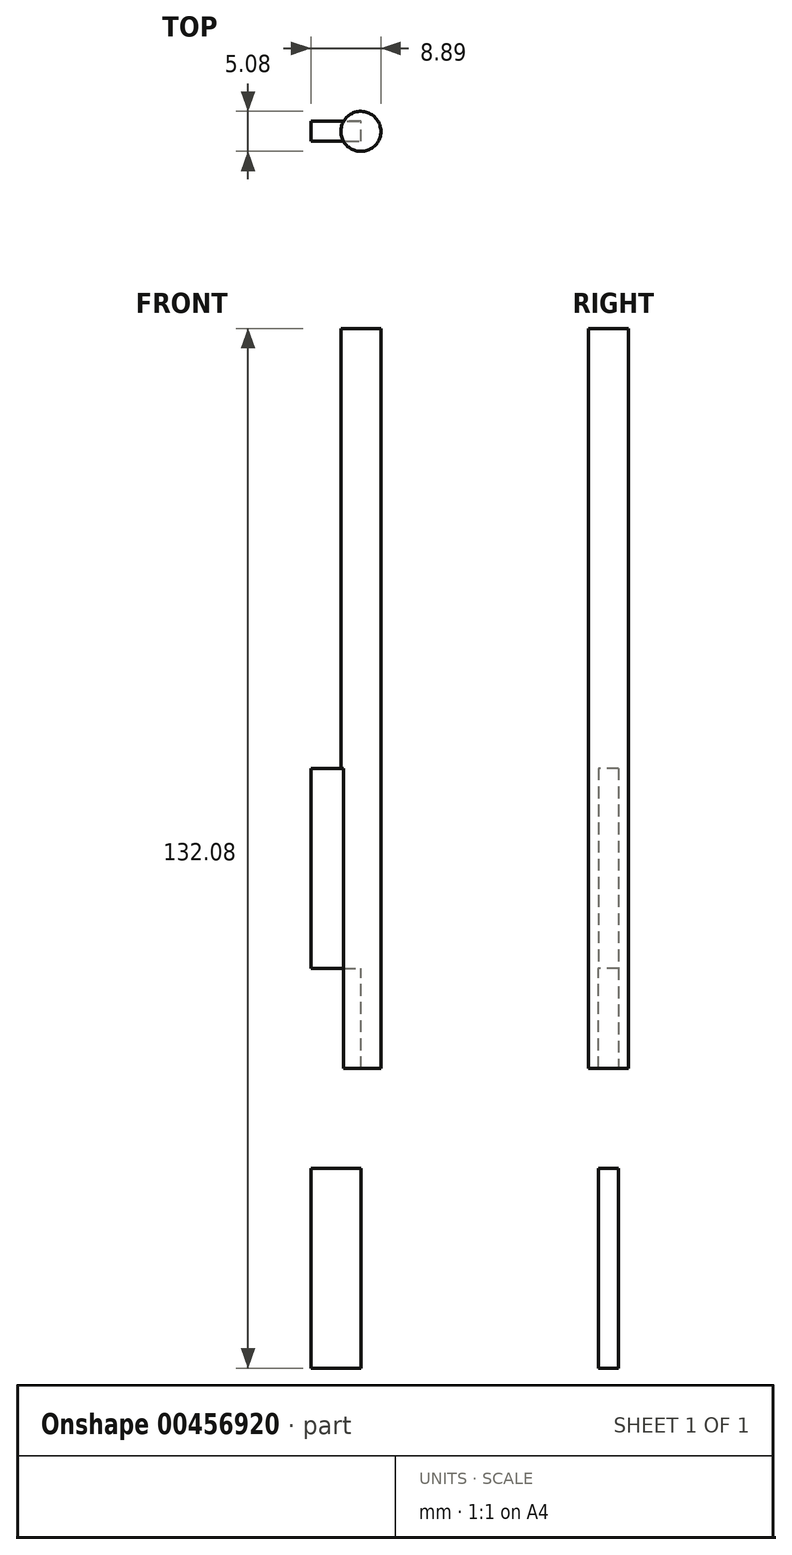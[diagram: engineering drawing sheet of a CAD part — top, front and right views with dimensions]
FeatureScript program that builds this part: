
annotation { "Feature Type Name" : "Feature", "Feature Type Description" : "" }
export const myFeature = defineFeature(function(context is Context, id is Id, definition is map)
    precondition{}
    {
        {
            var Q0;
            Q0=qCreatedBy(makeId("Top.planeOp"),FACE);
            var sketch = newSketch(context, id + "F0", { "sketchPlane" : qUnion([Q0])});
            skCircle(sketch, "E0", {"center": v(0, 0) * mm, "radius": 2.54 * mm});
            skSolve(sketch);
        }
        {
            var Q0;
            Q0=qCreatedBy(makeId("Top.planeOp"),FACE);
            var sketch = newSketch(context, id + "F1", { "sketchPlane" : qUnion([Q0])});
            skLineSegment(sketch, "E1.bottom", {"start": v(-6.35, 1.27) * mm, "end": v(0, 1.27) * mm});
            skLineSegment(sketch, "E1.top", {"start": v(-6.35, -1.27) * mm, "end": v(0, -1.27) * mm});
            skLineSegment(sketch, "E1.left", {"start": v(-6.35, 1.27) * mm, "end": v(-6.35, -1.27) * mm});
            skLineSegment(sketch, "E1.right", {"start": v(0, 1.27) * mm, "end": v(0, -1.27) * mm});
            skSolve(sketch);
        }
        {
            var Q0;
            Q0=makeQuery(id+"F0.imprint","IMPRINT",FACE,{"disambiguationData":[TD([[makeQuery(id+"F0.imprint","IMPRINT",EDGE,{"derivedFrom":sQuery(id+"F0.wireOp",EDGE,"E0")}),1.0]])]});
            extrude(context, id + "F2", {"entities" : qUnion([Q0]), "depth" : 50.8 * mm});
        }
        {
            var Q0;
            Q0=qSketchRegion(id+"F1",true);
            extrude(context, id + "F3", {"entities" : qUnion([Q0]), "operationType" : NewBodyOperationType.ADD, "endBound" : BoundingType.SYMMETRIC, "depth" : 76.2 * mm});
        }
        {
            var Q0;
            Q0=qSketchRegion(id+"F0",true);
            extrude(context, id + "F4", {"entities" : qUnion([Q0]), "operationType" : NewBodyOperationType.ADD, "depth" : 93.98 * mm});
        }
        {
            var Q0;
            Q0 = qConstructionFilter(qBodyType(qCreatedBy(id + "F0" ,EDGE), BodyType.WIRE), ConstructionObject.NO);
            extrude(context, id + "F5", {"bodyType" : ToolBodyType.SURFACE, "surfaceEntities" : qUnion([Q0]), "endBound" : BoundingType.SYMMETRIC, "depth" : 76.2 * mm});
        }
        {
            var Q0;
            Q0 = qSketchRegion(id + "F1", true);
            extrude(context, id + "F6", {"entities" : qUnion([Q0]), "operationType" : NewBodyOperationType.REMOVE, "endBound" : BoundingType.SYMMETRIC, "oppositeDirection" : true, "depth" : 25.4 * mm});
        }
    });
